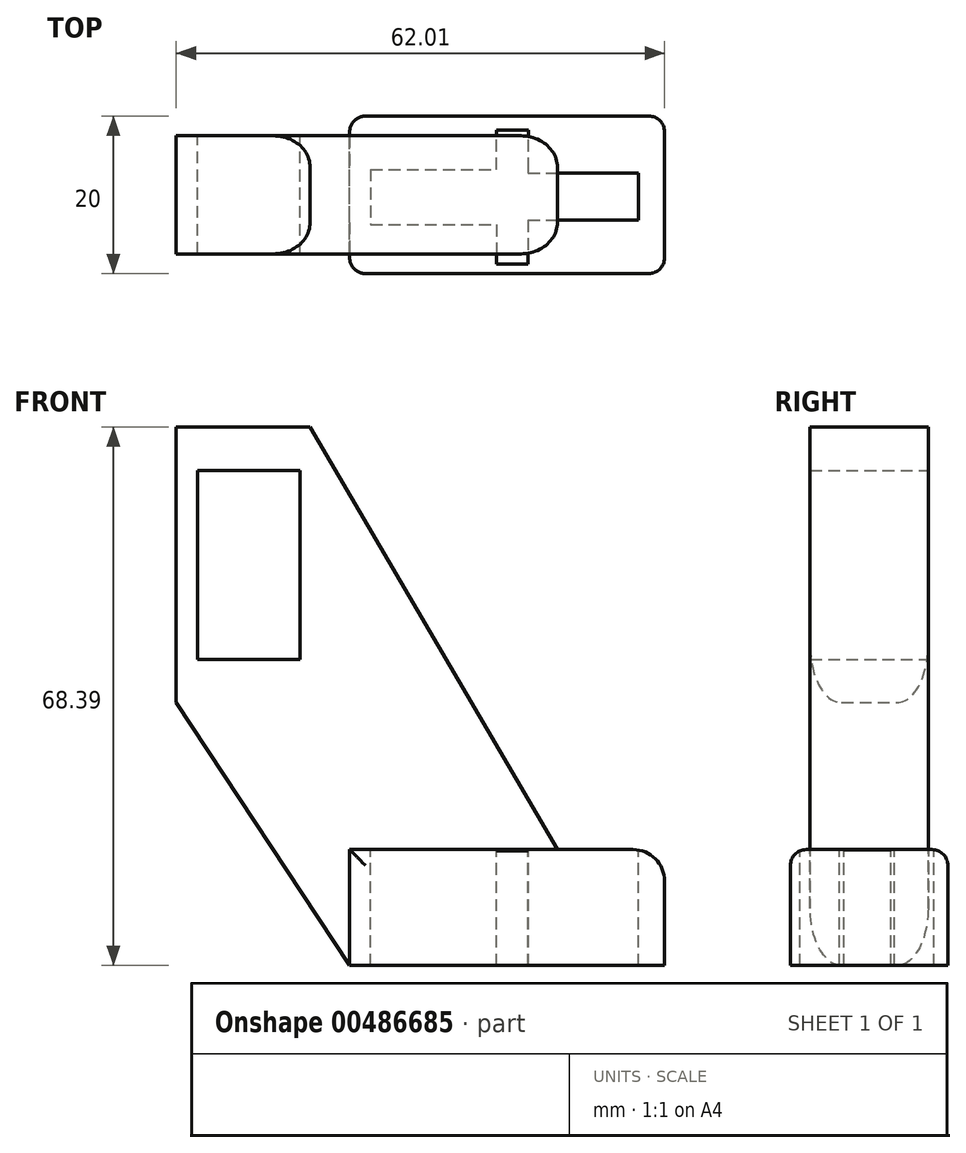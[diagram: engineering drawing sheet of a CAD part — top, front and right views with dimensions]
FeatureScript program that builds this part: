
annotation { "Feature Type Name" : "Feature", "Feature Type Description" : "" }
export const myFeature = defineFeature(function(context is Context, id is Id, definition is map)
    precondition{}
    {
        {
            var Q0;
            Q0=qCreatedBy(makeId("Front.planeOp"),FACE);
            var sketch = newSketch(context, id + "F0", { "sketchPlane" : qUnion([Q0])});
            skLineSegment(sketch, "E0", {"start": v(-13.77, -14.71) * mm, "end": v(21.23, -14.71) * mm});
            skLineSegment(sketch, "E1", {"start": v(-35.78, 53.68) * mm, "end": v(-35.78, 18.68) * mm});
            skLineSegment(sketch, "E2", {"start": v(-35.78, 18.68) * mm, "end": v(-13.77, -14.71) * mm});
            skLineSegment(sketch, "E3", {"start": v(-35.78, 53.68) * mm, "end": v(-18.78, 53.68) * mm});
            skLineSegment(sketch, "E4", {"start": v(-18.78, 53.68) * mm, "end": v(21.23, -14.71) * mm});
            skLineSegment(sketch, "E5.bottom", {"start": v(-20.09, 24.18) * mm, "end": v(-33.09, 24.18) * mm});
            skLineSegment(sketch, "E5.top", {"start": v(-20.09, 48.18) * mm, "end": v(-33.09, 48.18) * mm});
            skLineSegment(sketch, "E5.left", {"start": v(-20.09, 24.18) * mm, "end": v(-20.09, 48.18) * mm});
            skLineSegment(sketch, "E5.right", {"start": v(-33.09, 24.18) * mm, "end": v(-33.09, 48.18) * mm});
            skPoint(sketch, "E5.middle", {"position": v(-26.59, 36.18) * mm});
            skPoint(sketch, "E5.middle.positionSnap0", {"position": v(-35.78, 36.18) * mm});
            skPoint(sketch, "E5.centerSnap0", {"position": v(-35.78, 36.18) * mm});
            skLineSegment(sketch, "E6.bottom", {"start": v(-13.77, -14.71) * mm, "end": v(26.23, -14.71) * mm});
            skLineSegment(sketch, "E6.top", {"start": v(-13.77, 0) * mm, "end": v(26.23, 0) * mm});
            skLineSegment(sketch, "E6.left", {"start": v(-13.77, -14.71) * mm, "end": v(-13.77, 0) * mm});
            skLineSegment(sketch, "E6.right", {"start": v(26.23, -14.71) * mm, "end": v(26.23, 0) * mm});
            skSolve(sketch);
        }
        {
            var Q0;
            Q0=makeQuery(id+"F0.imprint","IMPRINT",FACE,{"disambiguationData":[TD([[makeQuery(id+"F0.imprint","IMPRINT",EDGE,{"derivedFrom":sQuery(id+"F0.wireOp",EDGE,"E1")}),1.0]])]});
            extrude(context, id + "F1", {"entities" : qUnion([Q0]), "depth" : 15 * mm});
        }
        {
            var Q0;
            {var subQ5=sQuery(id+"F0.wireOp",EDGE,"E6.right");Q0=makeQuery(id+"F0.imprint","IMPRINT",FACE,{"disambiguationData":[TD([[makeQuery(id+"F0.imprint","IMPRINT",EDGE,{"derivedFrom":subQ5}),1.0]])]});}
            var Q1;
            {var subQ5=sQuery(id+"F0.wireOp",EDGE,"E6.left");Q1=makeQuery(id+"F0.imprint","IMPRINT",FACE,{"disambiguationData":[TD([[makeQuery(id+"F0.imprint","IMPRINT",EDGE,{"derivedFrom":subQ5}),-1.0]])]});}
            extrude(context, id + "F2", {"entities" : qUnion([Q0, Q1]), "depth" : 17.5 * mm, "hasSecondDirection" : true, "secondDirectionOppositeDirection" : true, "secondDirectionDepth" : 2.5 * mm});
        }
        {
            var Q0;
            Q0=makeQuery(id+"F1.opExtrude","CAP_EDGE",EDGE,{"disambiguationData":[OSD([sQuery(id+"F0.wireOp",EDGE,"E4")])],"isStart":false});
            var Q1;
            Q1=makeQuery(id+"F1.opExtrude","CAP_EDGE",EDGE,{"disambiguationData":[OSD([sQuery(id+"F0.wireOp",EDGE,"E4")])],"isStart":true});
            var Q2;
            Q2=makeQuery(id+"F1.opExtrude","CAP_EDGE",EDGE,{"disambiguationData":[OSD([sQuery(id+"F0.wireOp",EDGE,"E2")])],"isStart":false});
            var Q3;
            Q3=makeQuery(id+"F1.opExtrude","CAP_EDGE",EDGE,{"disambiguationData":[OSD([sQuery(id+"F0.wireOp",EDGE,"E2")])],"isStart":true});
            var Q4;
            Q4=makeQuery(id+"F2.opExtrude","SWEPT_EDGE",EDGE,{"disambiguationData":[OSD([sQuery(id+"F0.wireOp",EDGE,"E6.top"),sQuery(id+"F0.wireOp",EDGE,"E6.right")])]});
            fillet(context, id + "F3", {"entities" : qUnion([Q0, Q1, Q2, Q3, Q4]), "radius" : 4 * mm, "tangentPropagation" : true, "allowEdgeOverflow" : false});
        }
        {
            var Q0;
            Q0=makeQuery(id+"F2.opExtrude","CAP_EDGE",EDGE,{"disambiguationData":[OSD([sQuery(id+"F0.wireOp",EDGE,"E6.top")])],"isStart":true});
            var Q1;
            Q1=makeQuery(id+"F2.opExtrude","CAP_EDGE",EDGE,{"disambiguationData":[OSD([sQuery(id+"F0.wireOp",EDGE,"E6.top")])],"isStart":false});
            var Q2;
            Q2=makeQuery(id+"F2.opExtrude","CAP_EDGE",EDGE,{"disambiguationData":[OSD([sQuery(id+"F0.wireOp",EDGE,"E6.left")])],"isStart":false});
            var Q3;
            Q3=makeQuery(id+"F2.opExtrude","CAP_EDGE",EDGE,{"disambiguationData":[OSD([sQuery(id+"F0.wireOp",EDGE,"E6.left")])],"isStart":true});
            fillet(context, id + "F4", {"entities" : qUnion([Q0, Q1, Q2, Q3]), "radius" : 2 * mm, "tangentPropagation" : true, "allowEdgeOverflow" : false});
        }
        {
            var Q0;
            Q0=qCreatedBy(makeId("Top.planeOp"),FACE);
            var sketch = newSketch(context, id + "F5", { "sketchPlane" : qUnion([Q0])});
            skLineSegment(sketch, "E7.bottom", {"start": v(-11.1, -4.28) * mm, "end": v(8.9, -4.28) * mm});
            skLineSegment(sketch, "E7.top", {"start": v(-11.1, -11.28) * mm, "end": v(8.9, -11.28) * mm});
            skLineSegment(sketch, "E7.left", {"start": v(-11.1, -4.28) * mm, "end": v(-11.1, -11.28) * mm});
            skLineSegment(sketch, "E7.right", {"start": v(8.9, -4.28) * mm, "end": v(8.9, -11.28) * mm});
            skLineSegment(sketch, "E8.bottom", {"start": v(8.9, -4.71) * mm, "end": v(22.9, -4.71) * mm});
            skLineSegment(sketch, "E8.top", {"start": v(8.9, -10.71) * mm, "end": v(22.9, -10.71) * mm});
            skLineSegment(sketch, "E8.left", {"start": v(8.9, -4.71) * mm, "end": v(8.9, -10.71) * mm});
            skLineSegment(sketch, "E8.right", {"start": v(22.9, -4.71) * mm, "end": v(22.9, -10.71) * mm});
            skLineSegment(sketch, "E9.bottom", {"start": v(8.9, -4.28) * mm, "end": v(4.9, -4.28) * mm});
            skLineSegment(sketch, "E9.top", {"start": v(8.9, -16.28) * mm, "end": v(4.9, -16.28) * mm});
            skLineSegment(sketch, "E9.left", {"start": v(8.9, -4.28) * mm, "end": v(8.9, -16.28) * mm});
            skLineSegment(sketch, "E9.right", {"start": v(4.9, -4.28) * mm, "end": v(4.9, -16.28) * mm});
            skLineSegment(sketch, "E10.bottom", {"start": v(4.9, -4.28) * mm, "end": v(8.97, -4.28) * mm});
            skLineSegment(sketch, "E10.top", {"start": v(4.9, 0.72) * mm, "end": v(8.97, 0.72) * mm});
            skLineSegment(sketch, "E10.left", {"start": v(4.9, -4.28) * mm, "end": v(4.9, 0.72) * mm});
            skLineSegment(sketch, "E10.right", {"start": v(8.97, -4.28) * mm, "end": v(8.97, 0.72) * mm});
            skSolve(sketch);
        }
        {
            var Q0;
            Q0 = qSketchRegion(id + "F5", true);
            extrude(context, id + "F6", {"entities" : qUnion([Q0]), "depth" : -15 * mm});
        }
        {
            var Q0;
            Q0=makeQuery(id+"F6.opExtrude","SWEPT_BODY",BODY,{"disambiguationData":[OSD([sQuery(id+"F5.wireOp",EDGE,"E7.bottom"),sQuery(id+"F5.wireOp",EDGE,"E7.top"),sQuery(id+"F5.wireOp",EDGE,"E7.left"),sQuery(id+"F5.wireOp",EDGE,"E8.bottom"),sQuery(id+"F5.wireOp",EDGE,"E8.top"),sQuery(id+"F5.wireOp",EDGE,"E8.right"),sQuery(id+"F5.wireOp",EDGE,"E9.top"),sQuery(id+"F5.wireOp",EDGE,"E9.left"),sQuery(id+"F5.wireOp",EDGE,"E9.right"),sQuery(id+"F5.wireOp",EDGE,"E10.bottom"),sQuery(id+"F5.wireOp",EDGE,"E10.top"),sQuery(id+"F5.wireOp",EDGE,"E10.left"),sQuery(id+"F5.wireOp",EDGE,"E10.right")])]});
            var Q1;
            Q1=makeQuery(id+"F2.opExtrude","SWEPT_BODY",BODY,{"disambiguationData":[OSD([sQuery(id+"F0.wireOp",EDGE,"E6.bottom"),sQuery(id+"F0.wireOp",EDGE,"E6.top"),sQuery(id+"F0.wireOp",EDGE,"E6.left"),sQuery(id+"F0.wireOp",EDGE,"E6.right")])]});
            booleanBodies(context, id + "F7", {"operationType" : BooleanOperationType.SUBTRACTION, "tools" : qUnion([Q0]), "targets" : qUnion([Q1])});
        }
    });
